# Revit family: Comfort Square Box Set Pan Cistern Mech Soft close Seat 8001
name_source: partatom
category: Plumbing Fixtures
units: mm (PartAtom-declared; Revit-internal decimal feet)

## family parameters
Always vertical = Yes
Cut with Voids When Loaded = No
Enable Cutting in Views = No
Host = Wall
Maintain Annotation Orientation = No
OmniClass Number = 23.45.00.00
OmniClass Title = Sanitary, Laundry, and Cleaning Equipment
Part Type = Normal
Room Calculation Point = No
Round Connector Dimension = Use Diameter
Shared = No

## types (1)
- Comfort Square Box Set Pan Cistern Mech Soft close Seat 8001 (Incl Pan Fixations)
    Actuator = Silver
    Category = Close Couple Box Sets
    Ceramic = White Ceramic
    Colour = White
    Default Elevation = 0 mm  [stored 0 ft]
    Depth = 620 mm  [stored 2.03412 ft]
    Fixing Details = Including Pan Fixings
    Height = 842 mm  [stored 2.76247 ft]
    Manufacturer = Lecico SA
    Material = Vitreous China
    Model = Comfort Square Box Set Pan Cistern Mech Soft close Seat 8001
    Plastic Clips = White Plastic
    Product Code = COMBOXDFLQSCSBE
    Technical Dimensions = W390 x H843 x D617mm
    URL = https://www.lecicosa.co.za
    Width = 382 mm

note: [stored X ft] marks values corroborated as IEEE doubles in the binary element streams (Revit-internal decimal feet)

## geometry (parser evidence)
native form markers: Blend x2, Sweep x3
no freeform markers — native parametric forms only
